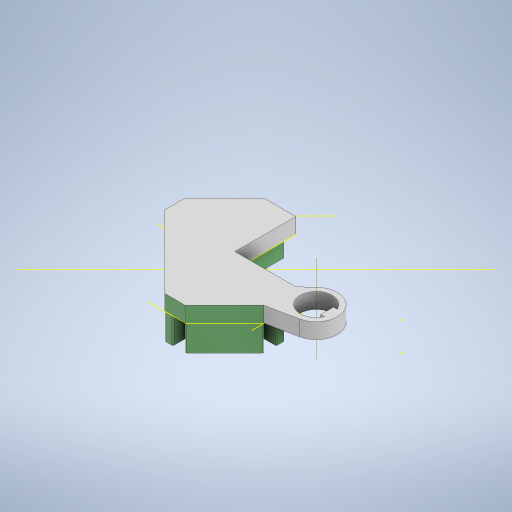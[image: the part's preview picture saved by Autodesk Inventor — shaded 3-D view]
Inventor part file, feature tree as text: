
AUTODESK INVENTOR PART (.ipt)
format: ipt  version: 2023 (Build 270158000, 158)  size: 395,264 bytes
history: native  units: in
note: dims shown in document units (in); Inventor stores cm internally (conversion verified against a paired STEP export)
features: other x5, sketch x3, extrude x1, plane x1
ambient origin geometry x8: Origin, YZ Plane, XZ Plane, XY Plane, X Axis, Y Axis, Z Axis, Center Point
bodies: Body1 (feature_tree)
feature tree (10):
  other  "potHolderLeft.ipt"
  extrude  "Extrusion1"  Depth=0.2441in
  other  "PLA2::potHolderLeft.ipt"
  other  "TaggingFeature1"
  sketch  "Sketch1"  dims[d0=0.3937in d1=0.2441in]
  sketch  "Sketch2"  dims[d2=0.0394in]
  plane  "Work Plane1"
  other  "Work Axis1"
  sketch  "Sketch3"  dims[d3=180.0deg d4=0.0492in d5=0.0394in d6=0.1181in d7=0.0in]
  other  "PLA2"
